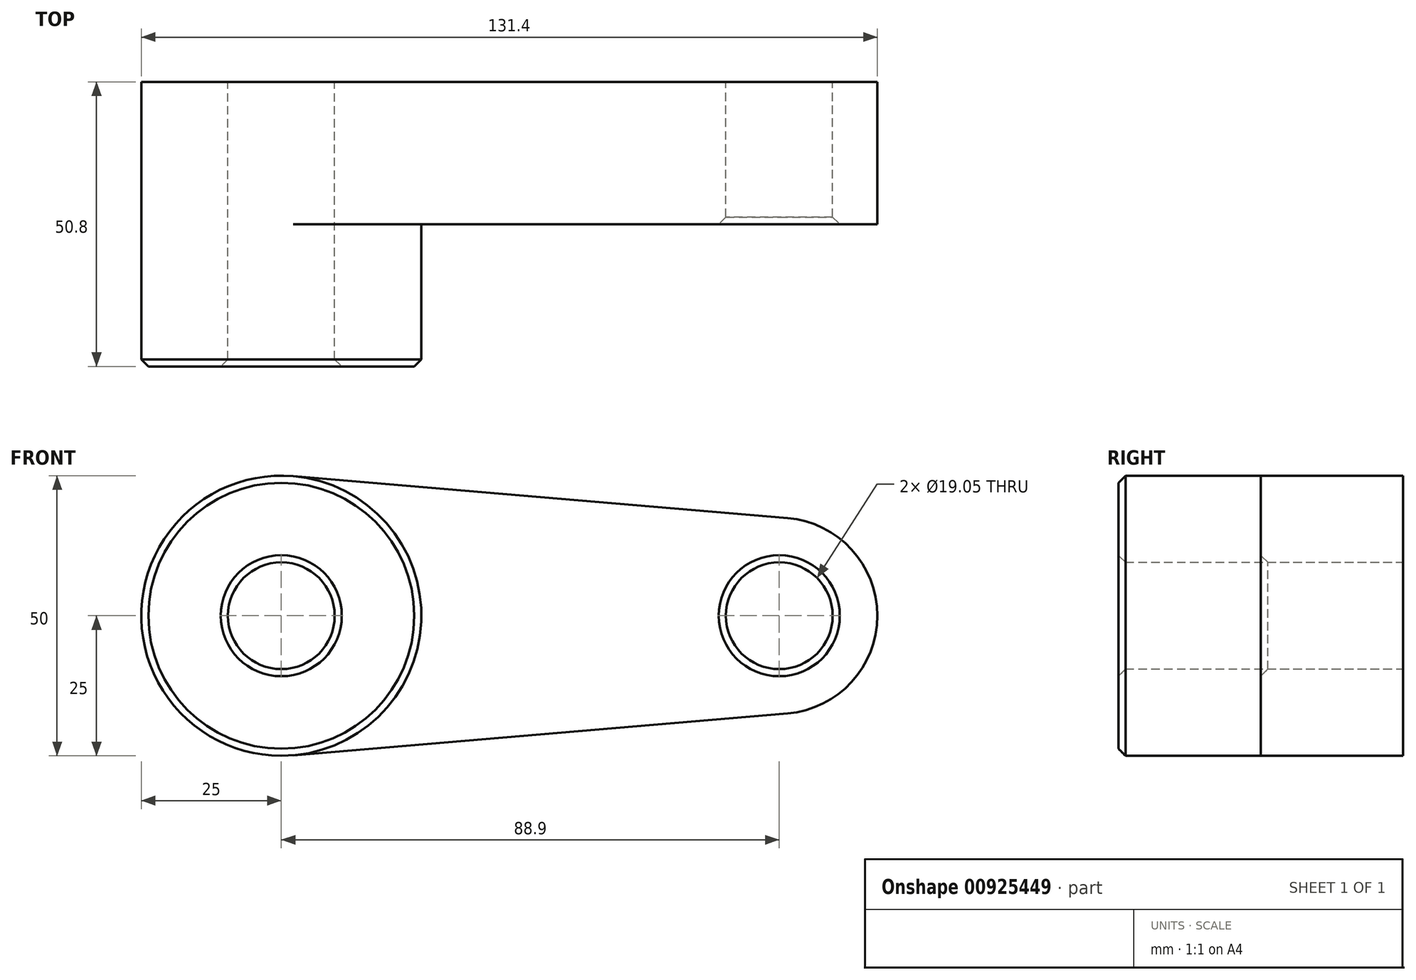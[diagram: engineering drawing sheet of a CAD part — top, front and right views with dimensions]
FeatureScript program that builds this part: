
annotation { "Feature Type Name" : "Feature", "Feature Type Description" : "" }
export const myFeature = defineFeature(function(context is Context, id is Id, definition is map)
    precondition{}
    {
        {
            var Q0;
            Q0=qCreatedBy(makeId("Front.planeOp"),FACE);
            var sketch = newSketch(context, id + "F0", { "sketchPlane" : qUnion([Q0])});
            skCircle(sketch, "E0", {"center": v(88.9, 0) * mm, "radius": 17.5 * mm});
            skLineSegment(sketch, "E1", {"start": v(2.1, 24.91) * mm, "end": v(90.38, 17.44) * mm});
            skLineSegment(sketch, "E2", {"start": v(2.1, -24.91) * mm, "end": v(90.38, -17.44) * mm});
            skCircle(sketch, "E3.converted", {"center": v(0, 0) * mm, "radius": 25 * mm});
            skCircle(sketch, "E4", {"center": v(0, 0) * mm, "radius": 9.53 * mm});
            skCircle(sketch, "E5", {"center": v(88.9, 0) * mm, "radius": 9.53 * mm});
            skSolve(sketch);
        }
        {
            var Q0;
            Q0 = qSketchRegion(id + "F0", true);
            extrude(context, id + "F1", {"entities" : qUnion([Q0]), "depth" : 25.4 * mm, "offsetDistance" : 25.4 * mm});
        }
        {
            var Q0;
            Q0=makeQuery(id+"F0.imprint","IMPRINT",FACE,{"disambiguationData":[TD([[makeQuery(id+"F0.imprint","IMPRINT",EDGE,{"derivedFrom":sQuery(id+"F0.wireOp",EDGE,"E4")}),-1.0]])]});
            extrude(context, id + "F2", {"entities" : qUnion([Q0]), "operationType" : NewBodyOperationType.ADD, "depth" : 50.8 * mm, "offsetDistance" : 25.4 * mm});
        }
        {
            var Q0;
            Q0=makeQuery(id+"F2.opExtrude","CAP_EDGE",EDGE,{"disambiguationData":[OSD([sQuery(id+"F0.wireOp",EDGE,"E4")])],"isStart":false});
            var Q1;
            Q1=makeQuery(id+"F2.opExtrude","CAP_EDGE",EDGE,{"disambiguationData":[OSD([sQuery(id+"F0.wireOp",EDGE,"E3.converted")])],"isStart":false});
            var Q2;
            Q2=makeQuery(id+"F1.opExtrude","CAP_EDGE",EDGE,{"disambiguationData":[OSD([sQuery(id+"F0.wireOp",EDGE,"E5")])],"isStart":false});
            chamfer(context, id + "F3", {"entities" : qUnion([Q0, Q1, Q2]), "width" : 1.27 * mm, "tangentPropagation" : true});
        }
    });
